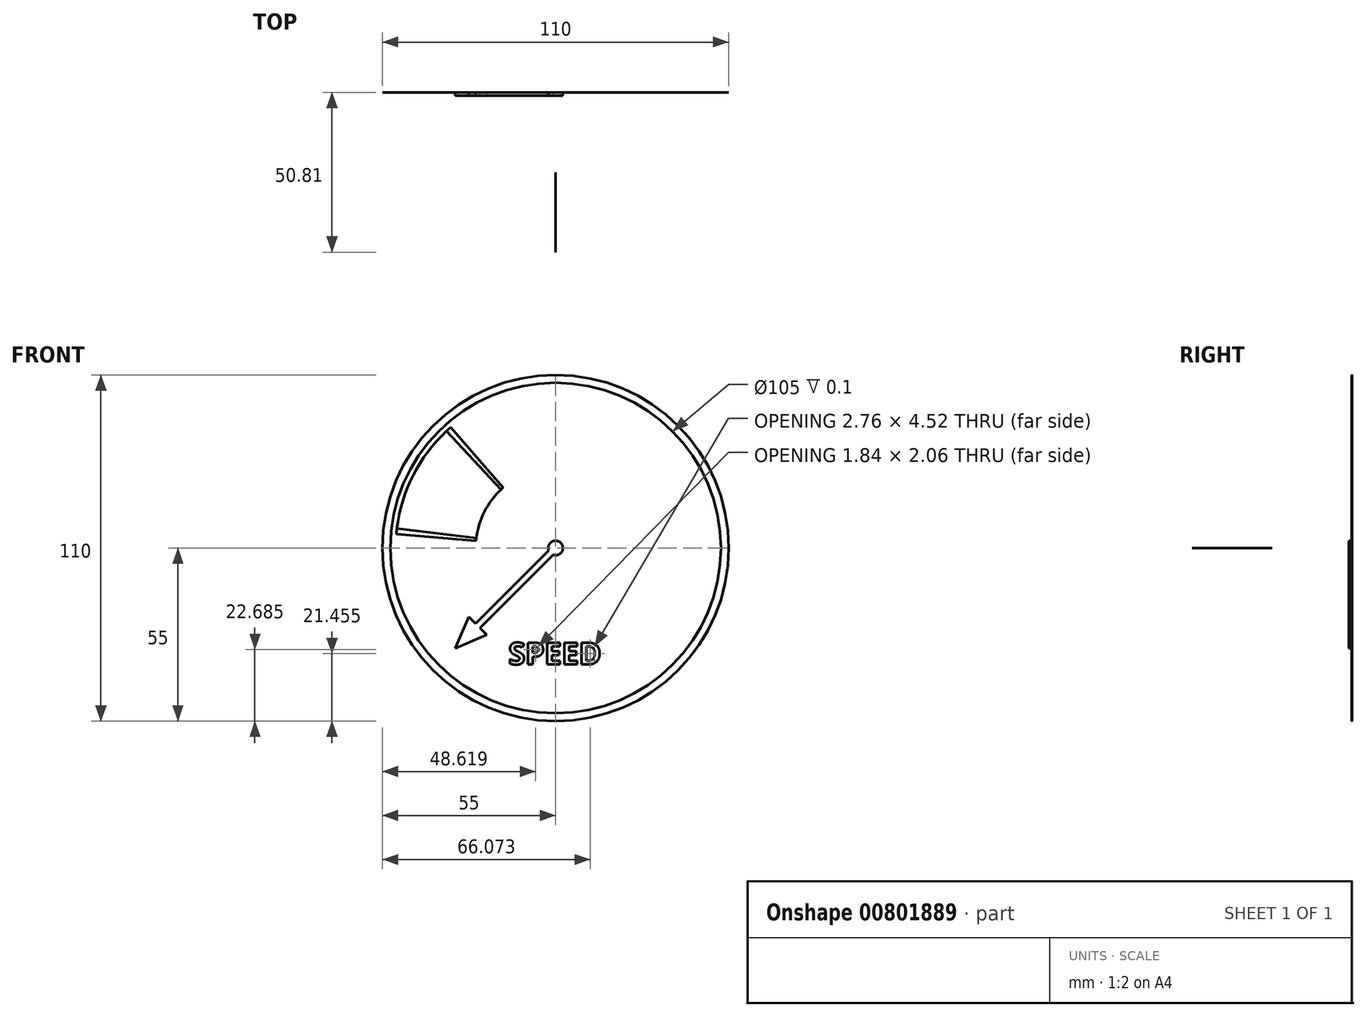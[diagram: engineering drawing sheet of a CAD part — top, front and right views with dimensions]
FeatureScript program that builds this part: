
annotation { "Feature Type Name" : "Feature", "Feature Type Description" : "" }
export const myFeature = defineFeature(function(context is Context, id is Id, definition is map)
    precondition{}
    {
        {
            var Q0;
            Q0=qCreatedBy(makeId("Right.planeOp"),FACE);
            var sketch = newSketch(context, id + "F0", { "sketchPlane" : qUnion([Q0])});
            skLineSegment(sketch, "E0", {"start": v(0, 0) * mm, "end": v(-116.06, 0) * mm, "construction": true});
            skSolve(sketch);
        }
        {
            var Q0;
            Q0=qCreatedBy(makeId("Right.planeOp"),FACE);
            var Q1;
            Q1=sQuery(id+"F0.wireOp",EDGE,"E0");
            cPlane(context, id + "F1", {"entities" : qUnion([Q0, Q1]), "cplaneType" : CPlaneType.LINE_ANGLE, "offset" : 25 * mm, "angle" : 135 * degree, "width" : 150 * mm, "height" : 150 * mm});
        }
        {
            var Q0;
            Q0=qCreatedBy(id+"F1.planeOp",FACE);
            var sketch = newSketch(context, id + "F2", { "sketchPlane" : qUnion([Q0])});
            skLineSegment(sketch, "E1.bottom", {"start": v(-25.4, 0) * mm, "end": v(-50.8, 0) * mm});
            skLineSegment(sketch, "E1.top", {"start": v(-25.4, 0) * mm, "end": v(-50.8, 0) * mm});
            skLineSegment(sketch, "E1.left", {"start": v(-25.4, 0) * mm, "end": v(-25.4, 0) * mm});
            skLineSegment(sketch, "E1.right", {"start": v(-50.8, 0) * mm, "end": v(-50.8, 0) * mm});
            skSolve(sketch);
        }
        {
            var Q0;
            Q0=qSketchRegion(id+"F2",true);
            var Q1;
            Q1=sQuery(id+"F0.wireOp",EDGE,"E0");
            revolve(context, id + "F3", {"surfaceOperationType" : NewSurfaceOperationType.NEW, "entities" : qUnion([Q0]), "axis" : qUnion([Q1]), "revolveType" : RevolveType.ONE_DIRECTION, "oppositeDirection" : true, "angle" : 50 * degree});
        }
        {
            var Q0;
            Q0=qCreatedBy(makeId("Right.planeOp"),FACE);
            var sketch = newSketch(context, id + "F4", { "sketchPlane" : qUnion([Q0])});
            skLineSegment(sketch, "E2.bottom", {"start": v(-0.01, 50.8) * mm, "end": v(0, 50.8) * mm});
            skLineSegment(sketch, "E2.top", {"start": v(-0.01, 25.4) * mm, "end": v(0, 25.4) * mm});
            skLineSegment(sketch, "E2.left", {"start": v(-0.01, 50.8) * mm, "end": v(0, 25.4) * mm});
            skLineSegment(sketch, "E2.right", {"start": v(0, 50.8) * mm, "end": v(0, 25.4) * mm});
            skSolve(sketch);
        }
        {
            var Q0;
            Q0=qSketchRegion(id+"F4",true);
            var Q1;
            Q1=sQuery(id+"F0.wireOp",EDGE,"E0");
            revolve(context, id + "F5", {"surfaceOperationType" : NewSurfaceOperationType.NEW, "entities" : qUnion([Q0]), "axis" : qUnion([Q1]), "revolveType" : RevolveType.ONE_DIRECTION, "oppositeDirection" : true, "angle" : 2 * degree});
        }
        {
            var Q0;
            Q0=qCreatedBy(makeId("Right.planeOp"),FACE);
            var Q1;
            Q1=sQuery(id+"F0.wireOp",EDGE,"E0");
            cPlane(context, id + "F6", {"entities" : qUnion([Q0, Q1]), "cplaneType" : CPlaneType.LINE_ANGLE, "offset" : 25 * mm, "angle" : 2 * degree, "oppositeDirection" : true, "width" : 150 * mm, "height" : 150 * mm});
        }
        {
            var Q0;
            Q0=qCreatedBy(id+"F6.planeOp",FACE);
            var sketch = newSketch(context, id + "F7", { "sketchPlane" : qUnion([Q0])});
            skLineSegment(sketch, "E3.bottom", {"start": v(0, 50.8) * mm, "end": v(0, 50.8) * mm});
            skLineSegment(sketch, "E3.top", {"start": v(0, 25.4) * mm, "end": v(0, 25.4) * mm});
            skLineSegment(sketch, "E3.left", {"start": v(0, 50.8) * mm, "end": v(0, 25.4) * mm});
            skLineSegment(sketch, "E3.right", {"start": v(0, 50.8) * mm, "end": v(0, 25.4) * mm});
            skSolve(sketch);
        }
        {
            var Q0;
            Q0=qSketchRegion(id+"F7",true);
            var Q1;
            Q1=sQuery(id+"F0.wireOp",EDGE,"E0");
            revolve(context, id + "F8", {"surfaceOperationType" : NewSurfaceOperationType.NEW, "entities" : qUnion([Q0]), "axis" : qUnion([Q1]), "revolveType" : RevolveType.ONE_DIRECTION, "oppositeDirection" : true, "angle" : 40 * degree});
        }
        {
            var Q0;
            Q0=qCreatedBy(makeId("Front.planeOp"),FACE);
            var sketch = newSketch(context, id + "F9", { "sketchPlane" : qUnion([Q0])});
            skLineSegment(sketch, "E4.bottom", {"start": v(-0.77, -2.19) * mm, "end": v(-24.04, -25.46) * mm});
            skLineSegment(sketch, "E4.top", {"start": v(-2.19, -0.77) * mm, "end": v(-25.46, -24.04) * mm});
            skPoint(sketch, "E4.middle", {"position": v(0, 0) * mm});
            skLineSegment(sketch, "E5", {"start": v(0, 0) * mm, "end": v(0, 10.99) * mm, "construction": true});
            skPoint(sketch, "E6", {"position": v(-24.75, -24.75) * mm});
            skCircle(sketch, "E7", {"center": v(-24.75, -24.75) * mm, "radius": 10.19 * mm, "construction": true});
            skLineSegment(sketch, "E8", {"start": v(-24.04, -25.46) * mm, "end": v(-21.92, -27.58) * mm});
            skLineSegment(sketch, "E9", {"start": v(-25.46, -24.04) * mm, "end": v(-27.58, -21.92) * mm});
            skLineSegment(sketch, "E10", {"start": v(-24.75, -24.75) * mm, "end": v(-31.95, -31.95) * mm, "construction": true});
            skLineSegment(sketch, "E11", {"start": v(-31.95, -31.95) * mm, "end": v(-27.58, -21.92) * mm});
            skLineSegment(sketch, "E12", {"start": v(-21.92, -27.58) * mm, "end": v(-31.95, -31.95) * mm});
            skArc(sketch, "E13", {"start": v(-0.77, -2.19) * mm, "mid": v(1.64, 1.64) * mm, "end": v(-2.19, -0.77) * mm});
            skPoint(sketch, "E14.orphan", {"position": v(-0.7, 0.7) * mm});
            skPoint(sketch, "E15.end.orphan", {"position": v(0.7, -0.7) * mm});
            skSolve(sketch);
        }
        {
            var Q0;
            Q0=qSketchRegion(id+"F9",true);
            extrude(context, id + "F10", {"entities" : qUnion([Q0]), "depth" : 1 * mm, "offsetDistance" : 25 * mm});
        }
        {
            var Q0;
            Q0=qCreatedBy(makeId("Front.planeOp"),FACE);
            var sketch = newSketch(context, id + "F11", { "sketchPlane" : qUnion([Q0])});
            skCircle(sketch, "E16", {"center": v(0, 0) * mm, "radius": 52.5 * mm});
            skCircle(sketch, "E17", {"center": v(0, 0) * mm, "radius": 55 * mm});
            skSolve(sketch);
        }
        {
            var Q0;
            Q0=qSketchRegion(id+"F11",true);
            extrude(context, id + "F12", {"entities" : qUnion([Q0]), "depth" : .1 * mm, "offsetDistance" : 25 * mm});
        }
        {
            var Q0;
            Q0=qCreatedBy(makeId("Front.planeOp"),FACE);
            var sketch = newSketch(context, id + "F13", { "sketchPlane" : qUnion([Q0])});
            skPoint(sketch, "E18.middle", {"position": v(68.26, -76.77) * mm});
            skText(sketch, "E19", { "text": "SPEED", "fontName": "OpenSans-Bold.ttf"});
            skLineSegment(sketch, "E20", {"start": v(0, 0) * mm, "end": v(0, -24.7) * mm, "construction": true});
            const initialGuessF13  = {"E19": [-0.015, -0.03702, 1, 0, 0.007]};
            skSetInitialGuess(sketch, initialGuessF13);
            skSolve(sketch);
        }
        {
            var Q0;
            Q0=qSketchRegion(id+"F13",true);
            extrude(context, id + "F14", {"entities" : qUnion([Q0]), "depth" : .1 * mm, "offsetDistance" : 25 * mm});
        }
        {
            var Q0;
            Q0=qCreatedBy(makeId("Front.planeOp"),FACE);
            var sketch = newSketch(context, id + "F15", { "sketchPlane" : qUnion([Q0])});
            skLineSegment(sketch, "E21", {"start": v(3.53, 25.15) * mm, "end": v(7.07, 50.3) * mm});
            skLineSegment(sketch, "E22", {"start": v(0, 0) * mm, "end": v(0, 18.46) * mm, "construction": true});
            skArc(sketch, "E23", {"start": v(3.53, 25.15) * mm, "mid": v(3.97, 25.09) * mm, "end": v(4.41, 25.01) * mm});
            skArc(sketch, "E24", {"start": v(7.07, 50.3) * mm, "mid": v(7.95, 50.17) * mm, "end": v(8.82, 50.03) * mm});
            skLineSegment(sketch, "E25", {"start": v(4.41, 25.01) * mm, "end": v(8.82, 50.03) * mm});
            skSolve(sketch);
        }
        {
            var Q0;
            Q0=qSketchRegion(id+"F15",true);
            extrude(context, id + "F16", {"entities" : qUnion([Q0]), "depth" : .1 * mm, "offsetDistance" : 25 * mm});
        }
        {
            var Q0;
            Q0=makeQuery(id+"F8.opRevolve","SWEPT_BODY",BODY,{"disambiguationData":[OSD([sQuery(id+"F7.wireOp",EDGE,"E3.bottom"),sQuery(id+"F7.wireOp",EDGE,"E3.top"),sQuery(id+"F7.wireOp",EDGE,"E3.left"),sQuery(id+"F7.wireOp",EDGE,"E3.right")])]});
            var Q1;
            Q1=makeQuery(id+"F16.opExtrude","SWEPT_BODY",BODY,{"disambiguationData":[OSD([sQuery(id+"F15.wireOp",EDGE,"E21"),sQuery(id+"F15.wireOp",EDGE,"E23"),sQuery(id+"F15.wireOp",EDGE,"E24"),sQuery(id+"F15.wireOp",EDGE,"E25")])]});
            var Q2;
            Q2=makeQuery(id+"F5.opRevolve","SWEPT_BODY",BODY,{"disambiguationData":[OSD([sQuery(id+"F4.wireOp",EDGE,"E2.bottom"),sQuery(id+"F4.wireOp",EDGE,"E2.top"),sQuery(id+"F4.wireOp",EDGE,"E2.left"),sQuery(id+"F4.wireOp",EDGE,"E2.right")])]});
            var Q3;
            Q3=sQuery(id+"F0.wireOp",EDGE,"E0");
            transform(context, id + "F17", {"entities" : qUnion([Q0, Q1, Q2]), "transformType" : TransformType.ROTATION, "transformAxis" : qUnion([Q3]), "angle" : 85 * degree, "makeCopy" : false});
        }
        {
            var Q0;
            Q0=makeQuery(id+"F16.opExtrude","SWEPT_BODY",BODY,{"disambiguationData":[OSD([sQuery(id+"F15.wireOp",EDGE,"E21"),sQuery(id+"F15.wireOp",EDGE,"E23"),sQuery(id+"F15.wireOp",EDGE,"E24"),sQuery(id+"F15.wireOp",EDGE,"E25")])]});
            var Q1;
            Q1=sQuery(id+"F0.wireOp",EDGE,"E0");
            transform(context, id + "F18", {"entities" : qUnion([Q0]), "transformType" : TransformType.ROTATION, "transformAxis" : qUnion([Q1]), "angle" : 34 * degree, "oppositeDirection" : true, "makeCopy" : false});
        }
    });
